FCSTD DOCUMENT  (FreeCAD 0.17R13541 (Git))
Label: PCB_Layout
License: All rights reserved
LicenseURL: http://en.wikipedia.org/wiki/All_rights_reserved
objects: TechDraw::DrawViewDimension×15, Sketcher::SketchObject×1, TechDraw::DrawSVGTemplate×1, TechDraw::DrawViewPart×1, TechDraw::DrawPage×1
note: 1 computed .brp shape members not serialized (recipe doc carries the construction recipe); baked Part::Feature solids carry a one-line shape summary decoded from their .brp

FEATURE [Sketcher::SketchObject] Sketch
  Placement = pos=(6,7,7) rot=(0,0,1;0rad)
  expr: Constraints[31] = 90 - 47.5 - 27
  sketch-geometry (12):
    g0: LineSegment StartX=-69.4184 StartY=38.5252 StartZ=0 EndX=20.5816 EndY=38.5252 EndZ=0
    g1: LineSegment StartX=20.5816 StartY=38.5252 StartZ=0 EndX=20.5816 EndY=-51.4748 EndZ=0
    g2: LineSegment StartX=20.5816 StartY=-51.4748 StartZ=0 EndX=-69.4184 EndY=-51.4748 EndZ=0
    g3: LineSegment StartX=-69.4184 StartY=-51.4748 StartZ=0 EndX=-69.4184 EndY=38.5252 EndZ=0
    g4: Circle CenterX=-64.4184 CenterY=33.5252 CenterZ=0 NormalX=0 NormalY=0 NormalZ=1 AngleXU=0 Radius=1.5
    g5: Circle CenterX=15.5816 CenterY=33.5252 CenterZ=0 NormalX=0 NormalY=0 NormalZ=1 AngleXU=0 Radius=1.5
    g6: Circle CenterX=-64.4184 CenterY=-36.4748 CenterZ=0 NormalX=0 NormalY=0 NormalZ=1 AngleXU=0 Radius=1.5
    g7: Circle CenterX=15.5816 CenterY=-46.4748 CenterZ=0 NormalX=0 NormalY=0 NormalZ=1 AngleXU=0 Radius=1.5
    g8: Circle CenterX=-58.4184 CenterY=11.5252 CenterZ=0 NormalX=0 NormalY=0 NormalZ=1 AngleXU=0 Radius=4.5
    g9: Circle CenterX=-49.4184 CenterY=-35.9748 CenterZ=0 NormalX=0 NormalY=0 NormalZ=1 AngleXU=0 Radius=4.5
    g10: Circle CenterX=-19.4184 CenterY=-35.9748 CenterZ=0 NormalX=0 NormalY=0 NormalZ=1 AngleXU=0 Radius=4.5
    g11: Circle CenterX=10.5816 CenterY=-35.9748 CenterZ=0 NormalX=0 NormalY=0 NormalZ=1 AngleXU=0 Radius=4.5
  constraints (34):
    c: Coincident(g0,g1)
    c: Coincident(g1,g2)
    c: Coincident(g2,g3)
    c: Coincident(g3,g0)
    c: Horizontal(g0)
    c: Horizontal(g2)
    c: Vertical(g1)
    c: Vertical(g3)
    c: DistanceX(g0,g0) = 90
    c: Radius(g4) = 1.5
    c: Radius(g5) = 1.5
    c: Radius(g6) = 1.5
    c: Radius(g7) = 1.5
    c: Distance(g4,g0) = 5
    c: Distance(g4,g3) = 5
    c: Distance(g5,g0) = 5
    c: Distance(g5,g1) = 5
    c: Distance(g7,g1) = 5
    c: Distance(g7,g2) = 5
    c: Distance(g6,g3) = 5
    c: Distance(g6,g2) = 15
    c: Radius(g8) = 4.5
    c: Radius(g9) = 4.5
    c: Radius(g10) = 4.5
    c: Radius(g11) = 4.5
    c: Distance(g8,g0) = 27
    c: Distance(g1) = 90
    c: Distance(g8,g3) = 11
    c: Distance(g9,g3) = 20
    c: Distance(g9,g10) = 30
    c: Distance(g10,g11) = 30
    c: Distance(g9,g2) = 15.5
    c: Distance(g10,g2) = 15.5
    c: Distance(g11,g2) = 15.5
FEATURE [TechDraw::DrawSVGTemplate] Template
  EditableTexts = Designed_by_Name=Jeremy Dahan; Drawing_number=Rev.3; FC-Date=21/02/2020; FC-SC=Scale; FC-SH=Sheet; FC-Title=Turntable PCB Layout; Subtitle=Subtitle; Weight=Weight
  Height = 210
  Orientation = 1
  Width = 297
FEATURE [TechDraw::DrawViewPart] View
  CoarseView = false
  Direction = (0,0,1)
  Focus = 100
  HardHidden = false
  IsoCount = 0
  IsoHidden = false
  IsoVisible = false
  LockPosition = false
  Perspective = false
  Rotation = 0
  ScaleType = 0
  SeamHidden = false
  SeamVisible = false
  SmoothHidden = false
  SmoothVisible = false
  Source = -> [Sketch]
  X = 113.971
  Y = 124.297
FEATURE [TechDraw::DrawViewDimension] Dimension005
  FormatSpec = %.1f
  LockPosition = false
  MeasureType = 1
  References2D = -> [View]
  Rotation = 0
  ScaleType = 0
  Type = 2
  X = -66.1949
  Y = 1.2779
FEATURE [TechDraw::DrawViewDimension] Dimension006
  FormatSpec = %.1f
  LockPosition = false
  MeasureType = 1
  References2D = -> [View]
  Rotation = 0
  ScaleType = 0
  Type = 1
  X = -2.94
  Y = 61.21
FEATURE [TechDraw::DrawViewDimension] Dimension007
  FormatSpec = %.1f
  LockPosition = false
  MeasureType = 1
  References2D = -> [View]
  Rotation = 0
  ScaleType = 0
  Type = 2
  X = -13.8013
  Y = -36.2922
FEATURE [TechDraw::DrawViewDimension] Dimension008
  FormatSpec = %.1f
  LockPosition = false
  MeasureType = 1
  References2D = -> [View]
  Rotation = 0
  ScaleType = 0
  Type = 1
  X = -12.14
  Y = -17.8905
FEATURE [TechDraw::DrawViewDimension] Dimension009
  FormatSpec = %.1f
  LockPosition = false
  MeasureType = 1
  References2D = -> [View]
  Rotation = 0
  ScaleType = 0
  Type = 1
  X = 20.3185
  Y = -17.7627
FEATURE [TechDraw::DrawViewDimension] Dimension010
  FormatSpec = %.1f
  LockPosition = false
  MeasureType = 1
  References2D = -> [View]
  Rotation = 0
  ScaleType = 0
  Type = 1
  X = -35.0143
  Y = -17.8905
FEATURE [TechDraw::DrawViewDimension] Dimension011
  FormatSpec = %.1f
  LockPosition = false
  MeasureType = 1
  References2D = -> [View]
  Rotation = 0
  ScaleType = 0
  Type = 0
  X = -37.8396
  Y = 7.42179
FEATURE [TechDraw::DrawViewDimension] Dimension012
  FormatSpec = %.1f
  LockPosition = false
  MeasureType = 1
  References2D = -> [View]
  Rotation = 0
  ScaleType = 0
  Type = 2
  X = -25.8135
  Y = 33.4808
FEATURE [TechDraw::DrawViewDimension] Dimension013
  FormatSpec = %.1f
  LockPosition = false
  MeasureType = 1
  References2D = -> [View]
  Rotation = 0
  ScaleType = 0
  Type = 2
  X = 50.6751
  Y = 53.1481
FEATURE [TechDraw::DrawViewDimension] Dimension014
  FormatSpec = %.1f
  LockPosition = false
  MeasureType = 1
  References2D = -> [View]
  Rotation = 0
  ScaleType = 0
  Type = 1
  X = 53.6381
  Y = 26.5507
FEATURE [TechDraw::DrawViewDimension] Dimension015
  FormatSpec = %.1f
  LockPosition = false
  MeasureType = 1
  References2D = -> [View]
  Rotation = 0
  ScaleType = 0
  Type = 2
  X = -52.7749
  Y = -37.2364
FEATURE [TechDraw::DrawViewDimension] Dimension016
  FormatSpec = %.1f
  LockPosition = false
  MeasureType = 1
  References2D = -> [View]
  Rotation = 0
  ScaleType = 0
  Type = 1
  X = -28.3693
  Y = -50.2979
FEATURE [TechDraw::DrawViewDimension] Dimension
  FormatSpec = %.1f
  LockPosition = false
  MeasureType = 1
  References2D = -> [View]
  Rotation = 0
  ScaleType = 0
  Type = 5
  X = 17.1136
  Y = 32.0189
FEATURE [TechDraw::DrawViewDimension] Dimension017
  FormatSpec = %.1f
  LockPosition = false
  MeasureType = 1
  References2D = -> [View]
  Rotation = 0
  ScaleType = 0
  Type = 5
  X = -11.8691
  Y = 11.3477
FEATURE [TechDraw::DrawViewDimension] Dimension018
  FormatSpec = %.1f
  LockPosition = false
  MeasureType = 1
  References2D = -> [View]
  Rotation = 0
  ScaleType = 0
  Type = 5
  X = 18.2483
  Y = -39.717
FEATURE [TechDraw::DrawPage] Page
  KeepUpdated = true
  ProjectionType = 0
  Template = -> Template
  Views = -> [View,Dimension005,Dimension006,Dimension007,Dimension008,Dimension009,Dimension010,Dimension011,Dimension012,Dimension013,Dimension014,Dimension015,Dimension016,Dimension,Dimension017,Dimension018]
